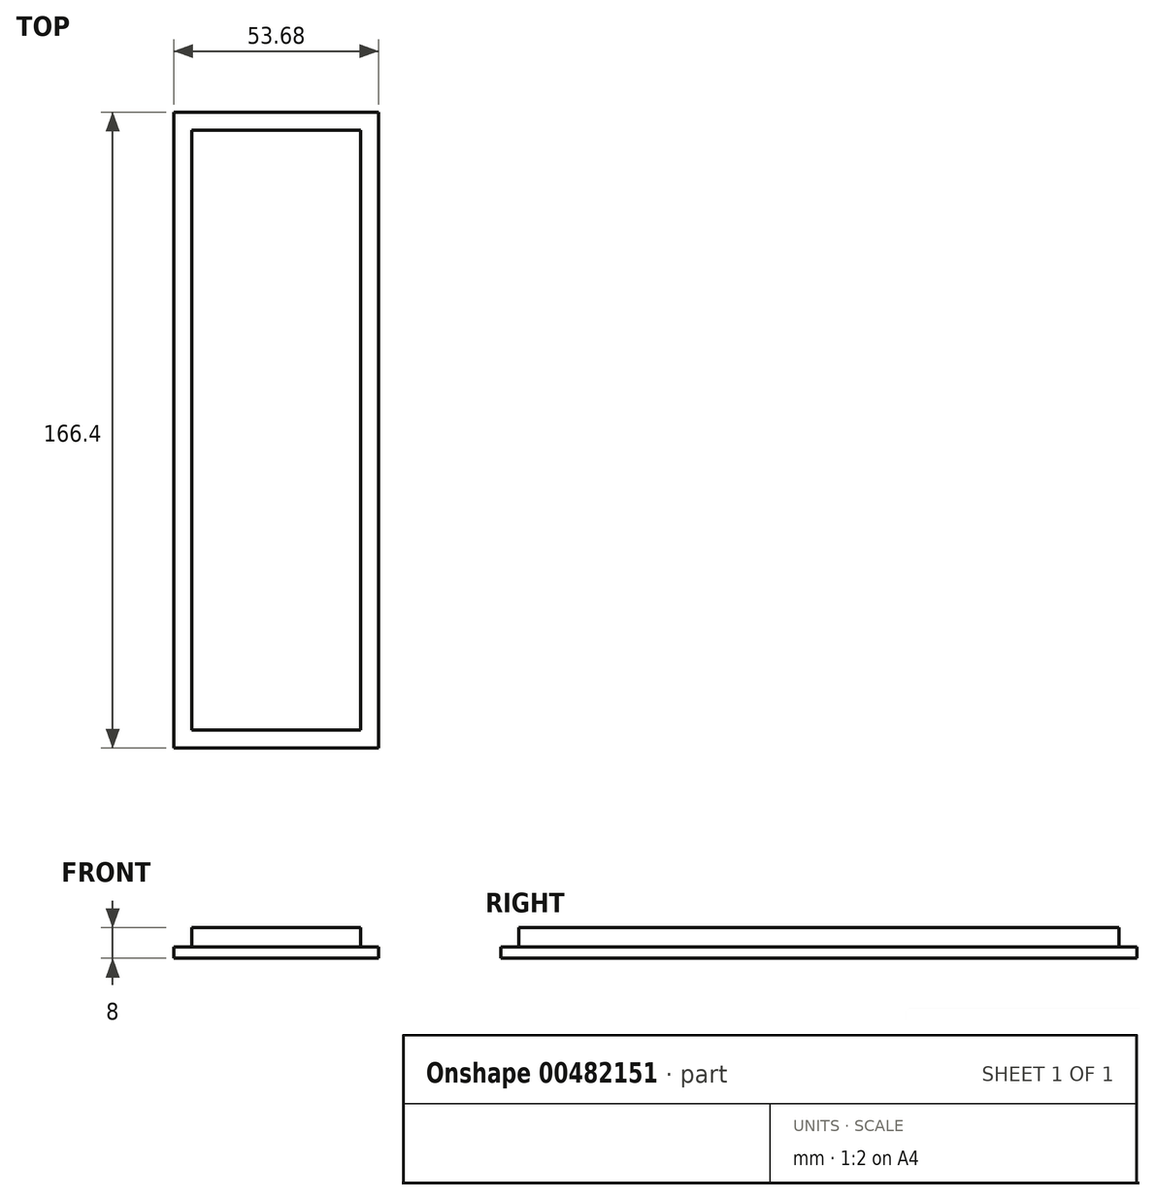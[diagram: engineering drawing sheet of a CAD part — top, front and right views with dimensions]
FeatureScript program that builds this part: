
annotation { "Feature Type Name" : "Feature", "Feature Type Description" : "" }
export const myFeature = defineFeature(function(context is Context, id is Id, definition is map)
    precondition{}
    {
        {
            var Q0;
            Q0=qCreatedBy(makeId("Top.planeOp"),FACE);
            var sketch = newSketch(context, id + "F0", { "sketchPlane" : qUnion([Q0])});
            skLineSegment(sketch, "E0.bottom", {"start": v(-22.14, 78.5) * mm, "end": v(22.13, 78.5) * mm});
            skLineSegment(sketch, "E0.top", {"start": v(-22.14, -78.5) * mm, "end": v(22.13, -78.5) * mm});
            skLineSegment(sketch, "E0.left", {"start": v(-22.14, 78.5) * mm, "end": v(-22.14, -78.5) * mm});
            skLineSegment(sketch, "E0.right", {"start": v(22.13, 78.5) * mm, "end": v(22.13, -78.5) * mm});
            skPoint(sketch, "E0.middle", {"position": v(0, 0) * mm});
            skLineSegment(sketch, "E1.0", {"start": v(-26.84, 83.2) * mm, "end": v(26.84, 83.2) * mm});
            skLineSegment(sketch, "E1.1", {"start": v(-26.84, 83.2) * mm, "end": v(-26.84, -83.2) * mm});
            skLineSegment(sketch, "E1.2", {"start": v(-26.84, -83.2) * mm, "end": v(26.84, -83.2) * mm});
            skLineSegment(sketch, "E1.3", {"start": v(26.84, 83.2) * mm, "end": v(26.84, -83.2) * mm});
            skSolve(sketch);
        }
        {
            var Q0;
            Q0 = qSketchRegion(id + "F0", true);
            var Q1;
            Q1=makeQuery(id+"F0.imprint","IMPRINT",FACE,{"disambiguationData":[TD([[makeQuery(id+"F0.imprint","IMPRINT",EDGE,{"derivedFrom":sQuery(id+"F0.wireOp",EDGE,"E0.bottom")}),-1.0]])]});
            extrude(context, id + "F1", {"entities" : qUnion([Q0, Q1]), "depth" : 3 * mm});
        }
        {
            var Q0;
            Q0=makeQuery(id+"F0.imprint","IMPRINT",FACE,{"disambiguationData":[TD([[makeQuery(id+"F0.imprint","IMPRINT",EDGE,{"derivedFrom":sQuery(id+"F0.wireOp",EDGE,"E0.bottom")}),-1.0]])]});
            extrude(context, id + "F2", {"entities" : qUnion([Q0]), "operationType" : NewBodyOperationType.ADD, "depth" : 8 * mm});
        }
    });
